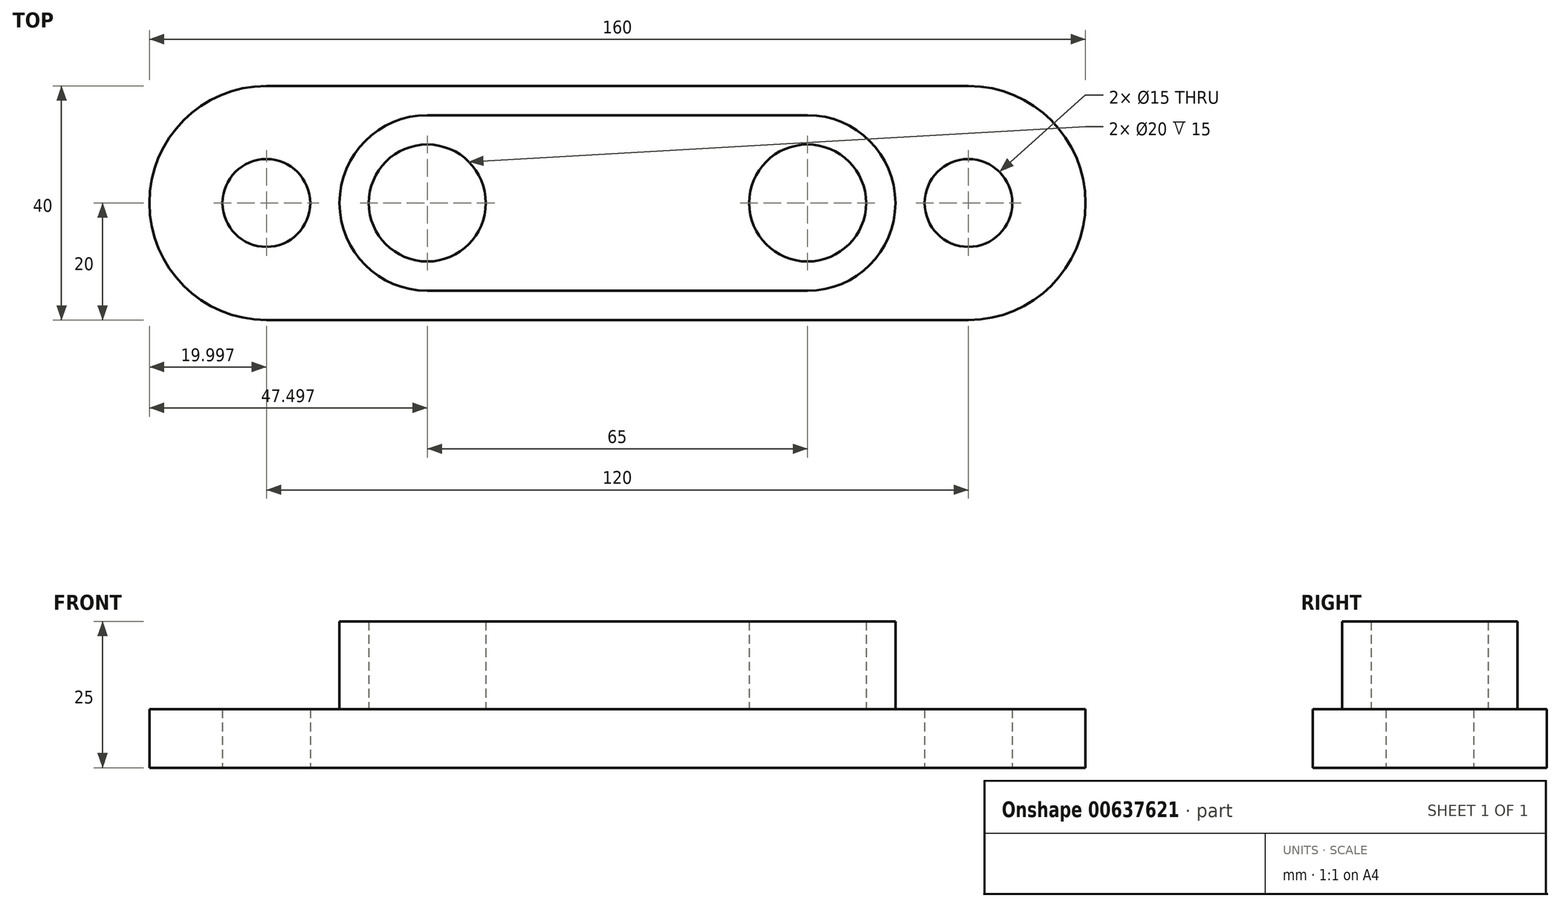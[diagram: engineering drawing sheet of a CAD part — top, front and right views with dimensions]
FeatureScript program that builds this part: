
annotation { "Feature Type Name" : "Feature", "Feature Type Description" : "" }
export const myFeature = defineFeature(function(context is Context, id is Id, definition is map)
    precondition{}
    {
        {
            var Q0;
            Q0=qCreatedBy(makeId("Top.planeOp"),FACE);
            var sketch = newSketch(context, id + "F0", { "sketchPlane" : qUnion([Q0])});
            skArc(sketch, "E0", {"start": v(-43.86, 20) * mm, "mid": v(-63.86, 0) * mm, "end": v(-43.86, -20) * mm});
            skArc(sketch, "E1", {"start": v(76.14, -20) * mm, "mid": v(96.14, 0) * mm, "end": v(76.14, 20) * mm});
            skLineSegment(sketch, "E2", {"start": v(-43.86, -20) * mm, "end": v(76.14, -20) * mm});
            skLineSegment(sketch, "E3", {"start": v(-43.86, 20) * mm, "end": v(76.14, 20) * mm});
            skCircle(sketch, "E4", {"center": v(-43.86, 0) * mm, "radius": 7.5 * mm});
            skCircle(sketch, "E5", {"center": v(76.14, 0) * mm, "radius": 7.5 * mm});
            skSolve(sketch);
        }
        {
            var Q0;
            Q0 = qSketchRegion(id + "F0", true);
            extrude(context, id + "F1", {"entities" : qUnion([Q0]), "depth" : 10 * mm, "offsetDistance" : 25 * mm});
        }
        {
            var Q0;
            Q0=qCreatedBy(makeId("Top.planeOp"),FACE);
            var sketch = newSketch(context, id + "F2", { "sketchPlane" : qUnion([Q0])});
            skArc(sketch, "E6", {"start": v(-16.36, 15) * mm, "mid": v(-31.36, 0) * mm, "end": v(-16.36, -15) * mm});
            skArc(sketch, "E7", {"start": v(48.64, -15) * mm, "mid": v(63.64, 0) * mm, "end": v(48.64, 15) * mm});
            skLineSegment(sketch, "E8", {"start": v(-16.36, 15) * mm, "end": v(48.64, 15) * mm});
            skLineSegment(sketch, "E9", {"start": v(-16.36, -15) * mm, "end": v(48.64, -15) * mm});
            skCircle(sketch, "E10", {"center": v(-16.36, 0) * mm, "radius": 10 * mm});
            skCircle(sketch, "E11", {"center": v(48.64, 0) * mm, "radius": 10 * mm});
            skSolve(sketch);
        }
        {
            var Q0;
            Q0 = qSketchRegion(id + "F2", true);
            extrude(context, id + "F3", {"entities" : qUnion([Q0]), "operationType" : NewBodyOperationType.ADD, "depth" : 25 * mm, "offsetDistance" : 25 * mm});
        }
    });
